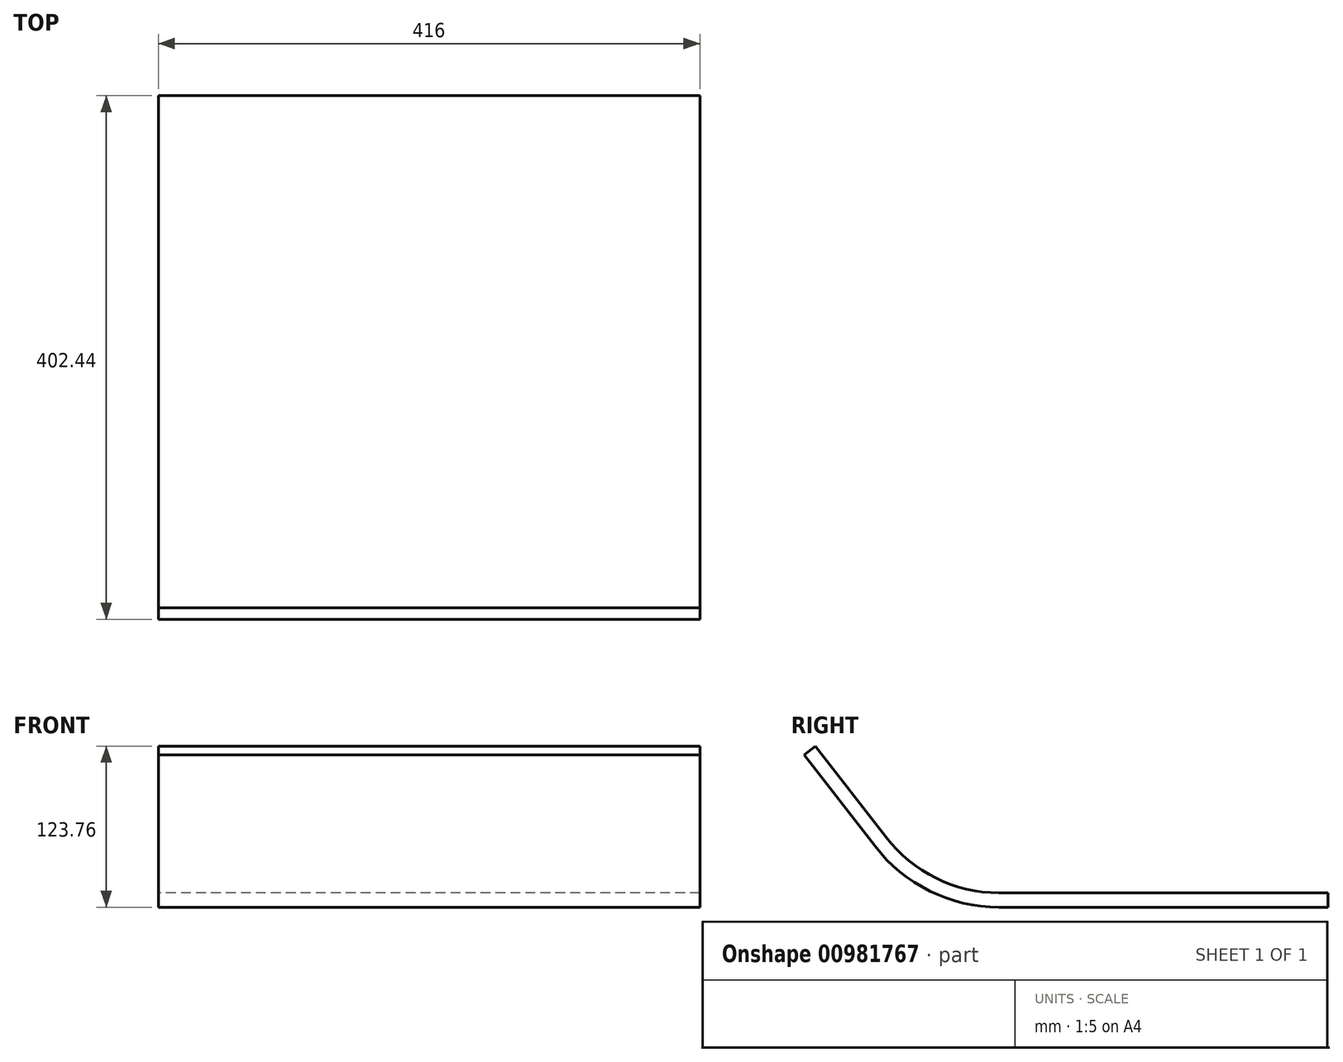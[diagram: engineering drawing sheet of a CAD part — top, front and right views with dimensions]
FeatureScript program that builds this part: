
annotation { "Feature Type Name" : "Feature", "Feature Type Description" : "" }
export const myFeature = defineFeature(function(context is Context, id is Id, definition is map)
    precondition{}
    {
        {
            var Q0;
            Q0=qCreatedBy(makeId("Right.planeOp"),FACE);
            var sketch = newSketch(context, id + "F0", { "sketchPlane" : qUnion([Q0])});
            skLineSegment(sketch, "E0", {"start": v(-51.67, -50.88) * mm, "end": v(201.22, -50.88) * mm});
            skLineSegment(sketch, "E1", {"start": v(-51.67, -61.88) * mm, "end": v(201.22, -61.88) * mm});
            skArc(sketch, "E2", {"start": v(-146.93, -14.85) * mm, "mid": v(-104.79, -49.48) * mm, "end": v(-51.67, -61.88) * mm});
            skArc(sketch, "E3", {"start": v(-138.22, -8.14) * mm, "mid": v(-99.93, -39.6) * mm, "end": v(-51.67, -50.88) * mm});
            skLineSegment(sketch, "E4", {"start": v(-146.93, -14.85) * mm, "end": v(-201.22, 55.13) * mm});
            skLineSegment(sketch, "E5", {"start": v(-138.22, -8.14) * mm, "end": v(-192.53, 61.88) * mm});
            skLineSegment(sketch, "E6", {"start": v(201.22, -61.88) * mm, "end": v(201.22, -50.88) * mm});
            skLineSegment(sketch, "E7", {"start": v(-192.53, 61.88) * mm, "end": v(-201.22, 55.13) * mm});
            skSolve(sketch);
        }
        {
            var Q0;
            Q0=makeQuery(id+"F0.imprint","IMPRINT",FACE,{"disambiguationData":[TD([[makeQuery(id+"F0.imprint","IMPRINT",EDGE,{"derivedFrom":sQuery(id+"F0.wireOp",EDGE,"E0")}),-1.0]])]});
            extrude(context, id + "F1", {"entities" : qUnion([Q0]), "depth" : 416 * mm, "offsetDistance" : 25 * mm});
        }
    });
